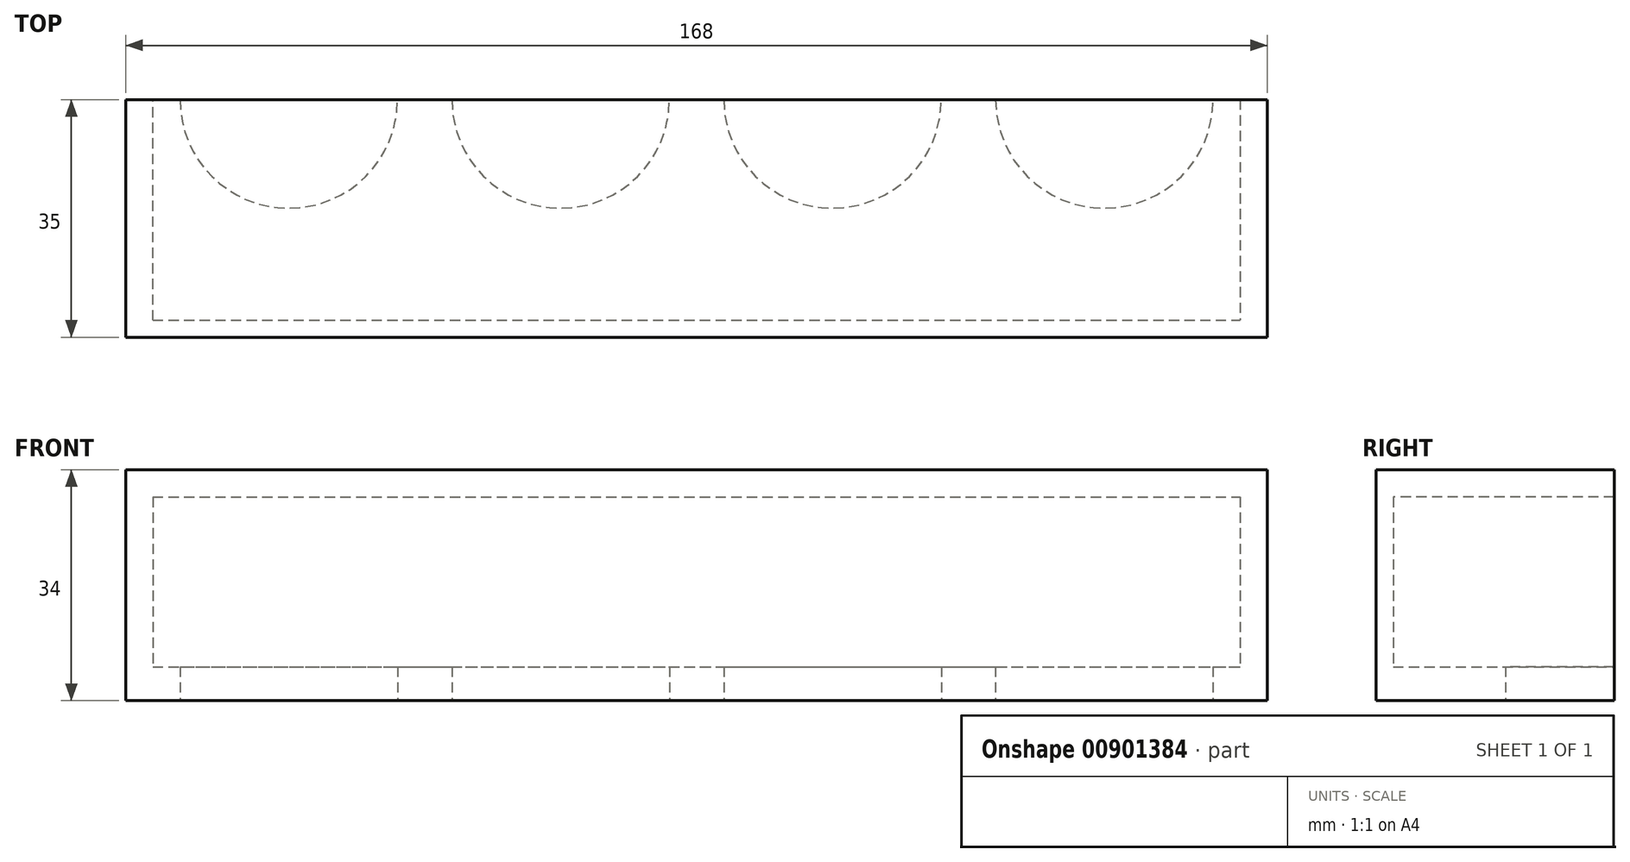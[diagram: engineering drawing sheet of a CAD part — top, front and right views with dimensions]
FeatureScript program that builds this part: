
annotation { "Feature Type Name" : "Feature", "Feature Type Description" : "" }
export const myFeature = defineFeature(function(context is Context, id is Id, definition is map)
    precondition{}
    {
        {
            var Q0;
            Q0=qCreatedBy(makeId("Top.planeOp"),FACE);
            var sketch = newSketch(context, id + "F0", { "sketchPlane" : qUnion([Q0])});
            skLineSegment(sketch, "E0", {"start": v(-60.9, 0) * mm, "end": v(-60.9, 20) * mm});
            skLineSegment(sketch, "E1", {"start": v(-60.9, 20) * mm, "end": v(89.1, 20) * mm});
            skLineSegment(sketch, "E2", {"start": v(-60.9, 20) * mm, "end": v(-40.9, 20) * mm});
            skCircle(sketch, "E3", {"center": v(-40.9, 20) * mm, "radius": 16 * mm});
            skLineSegment(sketch, "E4", {"start": v(-40.9, 20) * mm, "end": v(-0.9, 20) * mm});
            skCircle(sketch, "E5", {"center": v(-0.9, 20) * mm, "radius": 16 * mm});
            skLineSegment(sketch, "E6", {"start": v(-0.9, 20) * mm, "end": v(39.1, 20) * mm});
            skCircle(sketch, "E7", {"center": v(39.1, 20) * mm, "radius": 16 * mm});
            skLineSegment(sketch, "E8", {"start": v(39.1, 20) * mm, "end": v(79.1, 20) * mm});
            skCircle(sketch, "E9", {"center": v(79.1, 20) * mm, "radius": 16 * mm});
            skLineSegment(sketch, "E10", {"start": v(79.1, 20) * mm, "end": v(99.1, 20) * mm});
            skLineSegment(sketch, "E11", {"start": v(99.1, 20) * mm, "end": v(99.1, 0) * mm});
            skLineSegment(sketch, "E12", {"start": v(99.1, 0) * mm, "end": v(99.1, -15) * mm});
            skLineSegment(sketch, "E13", {"start": v(-60.9, 0) * mm, "end": v(-60.9, -15) * mm});
            skLineSegment(sketch, "E14", {"start": v(-60.9, -15) * mm, "end": v(99.1, -15) * mm});
            skSolve(sketch);
        }
        {
            var Q0;
            {var subQ14=sQuery(id+"F0.wireOp",EDGE,"E0");Q0=makeQuery(id+"F0.imprint","IMPRINT",FACE,{"disambiguationData":[TD([[makeQuery(id+"F0.imprint","IMPRINT",EDGE,{"derivedFrom":subQ14}),-1.0]])]});}
            extrude(context, id + "F1", {"entities" : qUnion([Q0]), "depth" : 5 * mm, "offsetDistance" : 25 * mm});
        }
        {
            var Q0;
            Q0=makeQuery(id+"F1.opExtrude","CAP_FACE",FACE,{"disambiguationData":[OSD([sQuery(id+"F0.wireOp",EDGE,"E0"),sQuery(id+"F0.wireOp",EDGE,"E2"),sQuery(id+"F0.wireOp",EDGE,"E3"),sQuery(id+"F0.wireOp",EDGE,"E4"),sQuery(id+"F0.wireOp",EDGE,"E5"),sQuery(id+"F0.wireOp",EDGE,"E6"),sQuery(id+"F0.wireOp",EDGE,"E7"),sQuery(id+"F0.wireOp",EDGE,"E8"),sQuery(id+"F0.wireOp",EDGE,"E9"),sQuery(id+"F0.wireOp",EDGE,"E10"),sQuery(id+"F0.wireOp",EDGE,"E11"),sQuery(id+"F0.wireOp",EDGE,"E12"),sQuery(id+"F0.wireOp",EDGE,"E13"),sQuery(id+"F0.wireOp",EDGE,"E14")])],"isStart":false});
            var sketch = newSketch(context, id + "F2", { "sketchPlane" : qUnion([Q0])});
            skLineSegment(sketch, "E15", {"start": v(-60.9, -15) * mm, "end": v(-60.9, -12.5) * mm});
            skLineSegment(sketch, "E16", {"start": v(-60.9, -12.5) * mm, "end": v(99.1, -12.5) * mm});
            skLineSegment(sketch, "E17", {"start": v(99.1, -12.5) * mm, "end": v(99.1, -15) * mm});
            skLineSegment(sketch, "E18", {"start": v(-60.9, -15) * mm, "end": v(99.1, -15) * mm});
            skSolve(sketch);
        }
        {
            var Q0;
            Q0=makeQuery(id+"F2.imprint","IMPRINT",FACE,{"disambiguationData":[TD([[makeQuery(id+"F2.imprint","IMPRINT",EDGE,{"derivedFrom":sQuery(id+"F2.wireOp",EDGE,"E16")}),-1.0]])]});
            extrude(context, id + "F3", {"entities" : qUnion([Q0]), "operationType" : NewBodyOperationType.ADD, "depth" : 25 * mm, "offsetDistance" : 25 * mm});
        }
        {
            var Q0;
            Q0=makeQuery(id+"F3.boolean.opBoolean","MERGE",FACE,{"derivedFrom":[makeQuery(id+"F1.opExtrude","SWEPT_FACE",FACE,{"disambiguationData":[OSD([sQuery(id+"F0.wireOp",EDGE,"E11"),sQuery(id+"F0.wireOp",EDGE,"E12")])]}),makeQuery(id+"F3.opExtrude","SWEPT_FACE",FACE,{"disambiguationData":[OSD([sQuery(id+"F2.wireOp",EDGE,"E17")])]})]});
            var sketch = newSketch(context, id + "F4", { "sketchPlane" : qUnion([Q0])});
            skLineSegment(sketch, "E19", {"start": v(-15, 30) * mm, "end": v(-15, 0) * mm});
            skLineSegment(sketch, "E20", {"start": v(20, 0) * mm, "end": v(-15, 0) * mm});
            skLineSegment(sketch, "E21", {"start": v(-15, 30) * mm, "end": v(20, 30) * mm});
            skLineSegment(sketch, "E22", {"start": v(20, 0) * mm, "end": v(20, 30) * mm});
            skSolve(sketch);
        }
        {
            var Q0;
            Q0 = qSketchRegion(id + "F4", true);
            extrude(context, id + "F5", {"entities" : qUnion([Q0]), "operationType" : NewBodyOperationType.ADD, "depth" : 4 * mm, "offsetDistance" : 25 * mm});
        }
        {
            var Q0;
            Q0=makeQuery(id+"F3.boolean.opBoolean","MERGE",FACE,{"derivedFrom":[makeQuery(id+"F1.opExtrude","SWEPT_FACE",FACE,{"disambiguationData":[OSD([sQuery(id+"F0.wireOp",EDGE,"E0"),sQuery(id+"F0.wireOp",EDGE,"E13")])]}),makeQuery(id+"F3.opExtrude","SWEPT_FACE",FACE,{"disambiguationData":[OSD([sQuery(id+"F2.wireOp",EDGE,"E15")])]})]});
            var sketch = newSketch(context, id + "F6", { "sketchPlane" : qUnion([Q0])});
            skLineSegment(sketch, "E23", {"start": v(-20, 0) * mm, "end": v(15, 0) * mm});
            skLineSegment(sketch, "E24", {"start": v(15, 0) * mm, "end": v(15, 30) * mm});
            skLineSegment(sketch, "E25", {"start": v(-20, 30) * mm, "end": v(15, 30) * mm});
            skLineSegment(sketch, "E26", {"start": v(-20, 30) * mm, "end": v(-20, 0) * mm});
            skSolve(sketch);
        }
        {
            var Q0;
            Q0 = qSketchRegion(id + "F6", true);
            extrude(context, id + "F7", {"entities" : qUnion([Q0]), "operationType" : NewBodyOperationType.ADD, "depth" : 4 * mm, "offsetDistance" : 25 * mm});
        }
        {
            var Q0;
            Q0=makeQuery(id+"F7.boolean.opBoolean","MERGE",FACE,{"derivedFrom":[makeQuery(id+"F5.boolean.opBoolean","MERGE",FACE,{"derivedFrom":[makeQuery(id+"F3.opExtrude","CAP_FACE",FACE,{"disambiguationData":[OSD([sQuery(id+"F2.wireOp",EDGE,"E16"),sQuery(id+"F2.wireOp",EDGE,"E17"),sQuery(id+"F2.wireOp",EDGE,"E15"),sQuery(id+"F2.wireOp",EDGE,"E18")])],"isStart":false}),makeQuery(id+"F5.opExtrude","SWEPT_FACE",FACE,{"disambiguationData":[OSD([sQuery(id+"F4.wireOp",EDGE,"E21")])]})]}),makeQuery(id+"F7.opExtrude","SWEPT_FACE",FACE,{"disambiguationData":[OSD([sQuery(id+"F6.wireOp",EDGE,"E25")])]})]});
            var sketch = newSketch(context, id + "F8", { "sketchPlane" : qUnion([Q0])});
            skLineSegment(sketch, "E27", {"start": v(-64.9, 20) * mm, "end": v(103.1, 20) * mm});
            skLineSegment(sketch, "E28", {"start": v(103.1, 20) * mm, "end": v(103.1, -15) * mm});
            skLineSegment(sketch, "E29", {"start": v(103.1, -15) * mm, "end": v(-64.9, -15) * mm});
            skLineSegment(sketch, "E30", {"start": v(-64.9, -15) * mm, "end": v(-64.9, 20) * mm});
            skSolve(sketch);
        }
        {
            var Q0;
            Q0 = qSketchRegion(id + "F8", true);
            extrude(context, id + "F9", {"entities" : qUnion([Q0]), "operationType" : NewBodyOperationType.ADD, "depth" : 4 * mm, "offsetDistance" : 25 * mm});
        }
    });
